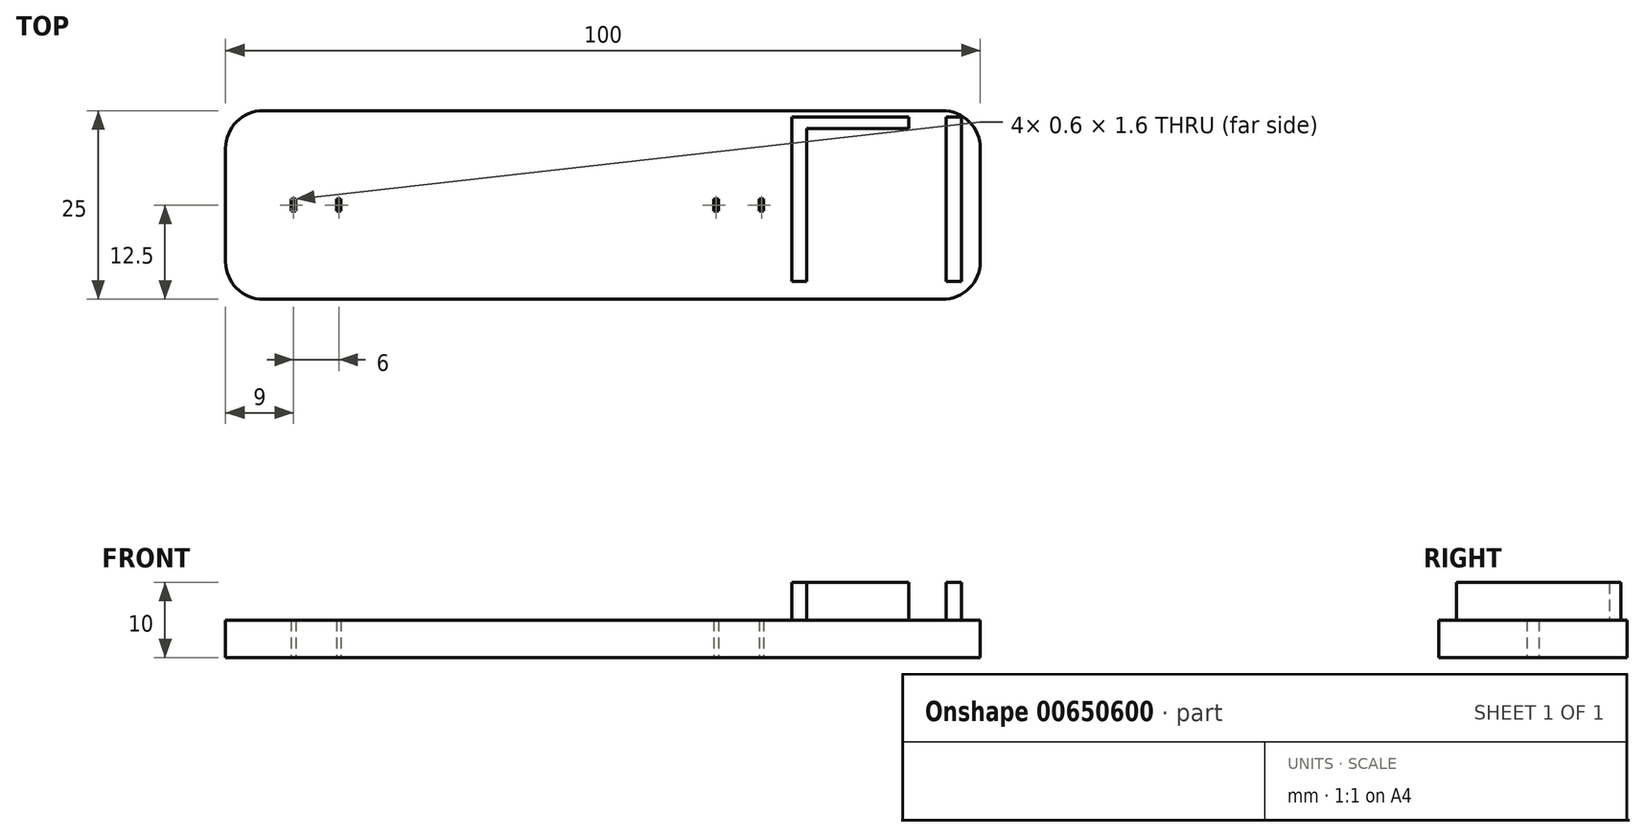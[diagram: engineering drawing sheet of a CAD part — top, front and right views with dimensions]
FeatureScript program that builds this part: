
annotation { "Feature Type Name" : "Feature", "Feature Type Description" : "" }
export const myFeature = defineFeature(function(context is Context, id is Id, definition is map)
    precondition{}
    {
        {
            var Q0;
            Q0=qCreatedBy(makeId("Top.planeOp"),FACE);
            var sketch = newSketch(context, id + "F0", { "sketchPlane" : qUnion([Q0])});
            skLineSegment(sketch, "E0.bottom", {"start": v(45, 12.5) * mm, "end": v(-45, 12.5) * mm});
            skLineSegment(sketch, "E0.top", {"start": v(45, -12.5) * mm, "end": v(-45, -12.5) * mm});
            skLineSegment(sketch, "E0.left", {"start": v(50, 7.5) * mm, "end": v(50, -7.5) * mm});
            skLineSegment(sketch, "E0.right", {"start": v(-50, 7.5) * mm, "end": v(-50, -7.5) * mm});
            skPoint(sketch, "E0.middle", {"position": v(0, 0) * mm});
            skPoint(sketch, "E1.visualSharp", {"position": v(-50, 12.5) * mm});
            skArc(sketch, "E1.filletArc", {"start": v(-45, 12.5) * mm, "mid": v(-48.54, 11.04) * mm, "end": v(-50, 7.5) * mm});
            skPoint(sketch, "E2.visualSharp", {"position": v(-50, -12.5) * mm});
            skArc(sketch, "E2.filletArc", {"start": v(-50, -7.5) * mm, "mid": v(-48.54, -11.04) * mm, "end": v(-45, -12.5) * mm});
            skPoint(sketch, "E3.visualSharp", {"position": v(50, 12.5) * mm});
            skArc(sketch, "E3.filletArc", {"start": v(50, 7.5) * mm, "mid": v(48.54, 11.04) * mm, "end": v(45, 12.5) * mm});
            skPoint(sketch, "E4.visualSharp", {"position": v(50, -12.5) * mm});
            skArc(sketch, "E4.filletArc", {"start": v(45, -12.5) * mm, "mid": v(48.54, -11.04) * mm, "end": v(50, -7.5) * mm});
            skLineSegment(sketch, "E5.bottom", {"start": v(-35.3, 0.8) * mm, "end": v(-34.7, 0.8) * mm});
            skLineSegment(sketch, "E5.top", {"start": v(-35.3, -0.8) * mm, "end": v(-34.7, -0.8) * mm});
            skLineSegment(sketch, "E5.left", {"start": v(-35.3, 0.8) * mm, "end": v(-35.3, -0.8) * mm});
            skLineSegment(sketch, "E5.right", {"start": v(-34.7, 0.8) * mm, "end": v(-34.7, -0.8) * mm});
            skPoint(sketch, "E5.middle", {"position": v(-35, 0) * mm});
            skLineSegment(sketch, "E6", {"start": v(-38, 1.75) * mm, "end": v(-38, -2.22) * mm, "construction": true});
            skLineSegment(sketch, "E7.MirrorCS", {"start": v(-40.7, 0.8) * mm, "end": v(-41.3, 0.8) * mm});
            skLineSegment(sketch, "E8.MirrorCS", {"start": v(-41.3, 0.8) * mm, "end": v(-41.3, -0.8) * mm});
            skLineSegment(sketch, "E9.MirrorCS", {"start": v(-40.7, 0.8) * mm, "end": v(-40.7, -0.8) * mm});
            skLineSegment(sketch, "E10.MirrorCS", {"start": v(-40.7, -0.8) * mm, "end": v(-41.3, -0.8) * mm});
            skLineSegment(sketch, "E11", {"start": v(-10, 3.8) * mm, "end": v(-10, -3.35) * mm, "construction": true});
            skLineSegment(sketch, "E12.MirrorCS", {"start": v(14.7, 0.8) * mm, "end": v(14.7, -0.8) * mm});
            skLineSegment(sketch, "E13.MirrorCS", {"start": v(15.3, 0.8) * mm, "end": v(15.3, -0.8) * mm});
            skLineSegment(sketch, "E14.MirrorCS", {"start": v(20.7, 0.8) * mm, "end": v(20.7, -0.8) * mm});
            skLineSegment(sketch, "E15.MirrorCS", {"start": v(21.3, 0.8) * mm, "end": v(21.3, -0.8) * mm});
            skLineSegment(sketch, "E16.MirrorCS", {"start": v(20.7, 0.8) * mm, "end": v(21.3, 0.8) * mm});
            skLineSegment(sketch, "E17.MirrorCS", {"start": v(20.7, -0.8) * mm, "end": v(21.3, -0.8) * mm});
            skLineSegment(sketch, "E18.MirrorCS", {"start": v(15.3, -0.8) * mm, "end": v(14.7, -0.8) * mm});
            skLineSegment(sketch, "E19.MirrorCS", {"start": v(15.3, 0.8) * mm, "end": v(14.7, 0.8) * mm});
            skSolve(sketch);
        }
        {
            var Q0;
            Q0 = qSketchRegion(id + "F0", true);
            extrude(context, id + "F1", {"entities" : qUnion([Q0]), "depth" : 5 * mm, "offsetDistance" : 25 * mm});
        }
        {
            var Q0;
            Q0=makeQuery(id+"F1.opExtrude","CAP_FACE",FACE,{"disambiguationData":[OSD([sQuery(id+"F0.wireOp",EDGE,"E0.bottom"),sQuery(id+"F0.wireOp",EDGE,"E0.top"),sQuery(id+"F0.wireOp",EDGE,"E0.left"),sQuery(id+"F0.wireOp",EDGE,"E0.right"),sQuery(id+"F0.wireOp",EDGE,"E1.filletArc"),sQuery(id+"F0.wireOp",EDGE,"E2.filletArc"),sQuery(id+"F0.wireOp",EDGE,"E3.filletArc"),sQuery(id+"F0.wireOp",EDGE,"E4.filletArc"),sQuery(id+"F0.wireOp",EDGE,"E5.bottom"),sQuery(id+"F0.wireOp",EDGE,"E5.top"),sQuery(id+"F0.wireOp",EDGE,"E5.left"),sQuery(id+"F0.wireOp",EDGE,"E5.right"),sQuery(id+"F0.wireOp",EDGE,"E7.MirrorCS"),sQuery(id+"F0.wireOp",EDGE,"E8.MirrorCS"),sQuery(id+"F0.wireOp",EDGE,"E9.MirrorCS"),sQuery(id+"F0.wireOp",EDGE,"E10.MirrorCS"),sQuery(id+"F0.wireOp",EDGE,"E12.MirrorCS"),sQuery(id+"F0.wireOp",EDGE,"E13.MirrorCS"),sQuery(id+"F0.wireOp",EDGE,"E14.MirrorCS"),sQuery(id+"F0.wireOp",EDGE,"E15.MirrorCS"),sQuery(id+"F0.wireOp",EDGE,"E16.MirrorCS"),sQuery(id+"F0.wireOp",EDGE,"E17.MirrorCS"),sQuery(id+"F0.wireOp",EDGE,"E18.MirrorCS"),sQuery(id+"F0.wireOp",EDGE,"E19.MirrorCS")])],"isStart":false});
            var sketch = newSketch(context, id + "F2", { "sketchPlane" : qUnion([Q0])});
            skLineSegment(sketch, "E20.top", {"start": v(27, -10.15) * mm, "end": v(25, -10.15) * mm});
            skLineSegment(sketch, "E20.left", {"start": v(27, 10.15) * mm, "end": v(27, -10.15) * mm});
            skLineSegment(sketch, "E20.right", {"start": v(25, 10.15) * mm, "end": v(25, -10.15) * mm});
            skPoint(sketch, "E20.middle", {"position": v(26, 0) * mm});
            skLineSegment(sketch, "E21.top", {"start": v(47.5, -10.15) * mm, "end": v(45.5, -10.15) * mm});
            skLineSegment(sketch, "E21.left", {"start": v(47.5, 10.15) * mm, "end": v(47.5, -10.15) * mm});
            skLineSegment(sketch, "E21.right", {"start": v(45.5, 10.15) * mm, "end": v(45.5, -10.15) * mm});
            skPoint(sketch, "E21.middle", {"position": v(46.5, 0) * mm});
            skLineSegment(sketch, "E22.bottom", {"start": v(25, 11.65) * mm, "end": v(47.5, 11.65) * mm});
            skLineSegment(sketch, "E22.top", {"start": v(27, 10.15) * mm, "end": v(45.5, 10.15) * mm});
            skLineSegment(sketch, "E22.left", {"start": v(25, 11.65) * mm, "end": v(25, 10.15) * mm});
            skLineSegment(sketch, "E22.right", {"start": v(47.5, 11.65) * mm, "end": v(47.5, 10.15) * mm});
            skSolve(sketch);
        }
        {
            var Q0;
            Q0 = qSketchRegion(id + "F2", true);
            extrude(context, id + "F3", {"entities" : qUnion([Q0]), "operationType" : NewBodyOperationType.ADD, "depth" : 5 * mm, "offsetDistance" : 25 * mm});
        }
        {
            var Q0;
            Q0=makeQuery(id+"F3.opExtrude","SWEPT_FACE",FACE,{"disambiguationData":[OSD([sQuery(id+"F2.wireOp",EDGE,"E22.bottom")])]});
            var sketch = newSketch(context, id + "F4", { "sketchPlane" : qUnion([Q0])});
            skLineSegment(sketch, "E23.bottom", {"start": v(-45.5, 10) * mm, "end": v(-40.5, 10) * mm});
            skLineSegment(sketch, "E23.top", {"start": v(-45.5, 5) * mm, "end": v(-40.5, 5) * mm});
            skLineSegment(sketch, "E23.left", {"start": v(-45.5, 10) * mm, "end": v(-45.5, 5) * mm});
            skLineSegment(sketch, "E23.right", {"start": v(-40.5, 10) * mm, "end": v(-40.5, 5) * mm});
            skSolve(sketch);
        }
        {
            var Q0;
            Q0 = qSketchRegion(id + "F4", true);
            extrude(context, id + "F5", {"entities" : qUnion([Q0]), "operationType" : NewBodyOperationType.REMOVE, "oppositeDirection" : true, "depth" : 25 * mm, "offsetDistance" : 25 * mm});
        }
    });
